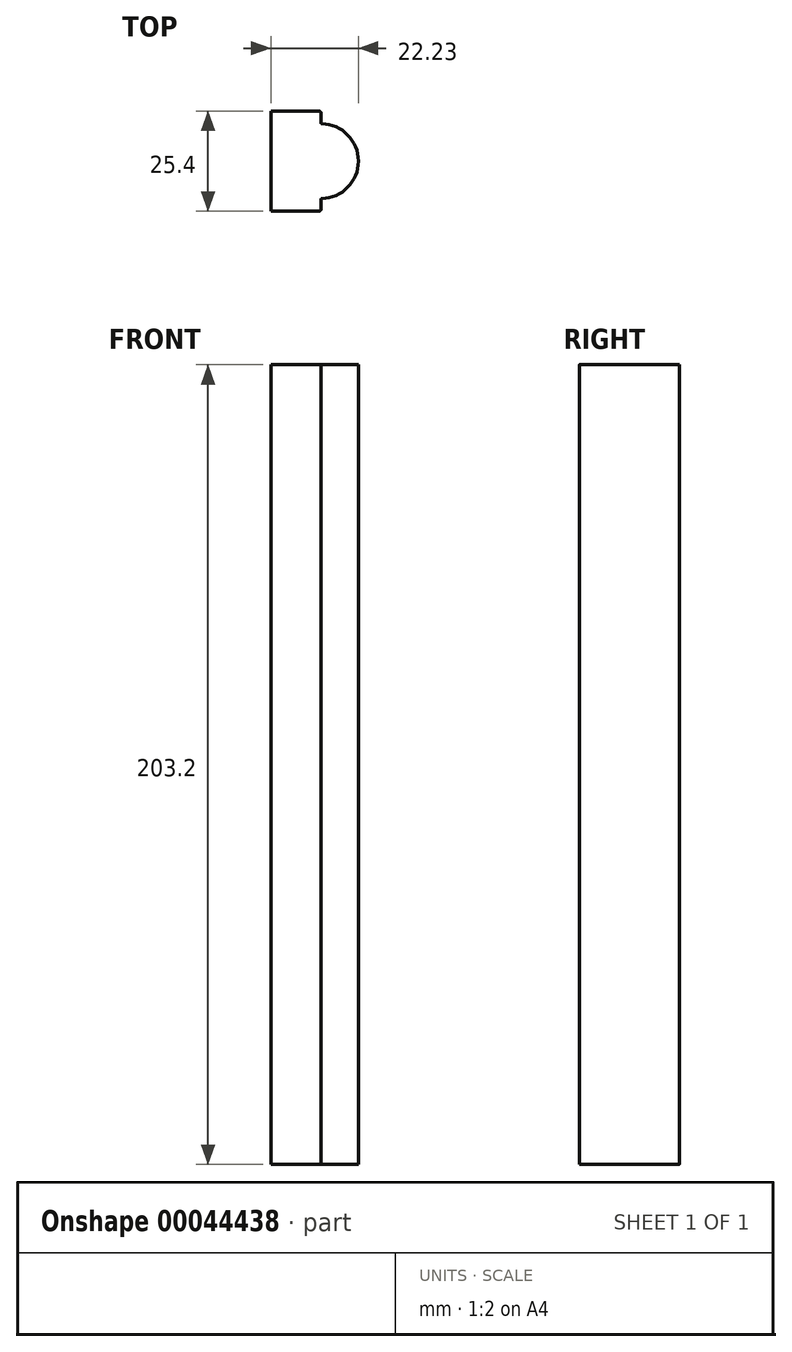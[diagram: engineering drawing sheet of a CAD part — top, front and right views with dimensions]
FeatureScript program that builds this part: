
annotation { "Feature Type Name" : "Feature", "Feature Type Description" : "" }
export const myFeature = defineFeature(function(context is Context, id is Id, definition is map)
    precondition{}
    {
        {
            var Q0;
            Q0=qCreatedBy(makeId("Top.planeOp"),FACE);
            var sketch = newSketch(context, id + "F0", { "sketchPlane" : qUnion([Q0])});
            skArc(sketch, "E0", {"start": v(0, -9.53) * mm, "mid": v(9.53, 0) * mm, "end": v(0, 9.53) * mm});
            skLineSegment(sketch, "E1", {"start": v(0, 9.53) * mm, "end": v(0, 12.7) * mm});
            skLineSegment(sketch, "E2", {"start": v(0, 12.7) * mm, "end": v(-12.7, 12.7) * mm});
            skLineSegment(sketch, "E3", {"start": v(-12.7, 12.7) * mm, "end": v(-12.7, -12.7) * mm});
            skLineSegment(sketch, "E4", {"start": v(-12.7, -12.7) * mm, "end": v(0, -12.7) * mm});
            skLineSegment(sketch, "E5", {"start": v(0, -12.7) * mm, "end": v(0, -9.53) * mm});
            skSolve(sketch);
        }
        {
            var Q0;
            Q0 = qSketchRegion(id + "F0", true);
            extrude(context, id + "F1", {"entities" : qUnion([Q0]), "depth" : 203.2 * mm});
        }
        {
            var Q0;
            Q0=makeQuery(id+"F1.opExtrude","SWEPT_EDGE",EDGE,{"disambiguationData":[OSD([sQuery(id+"F0.wireOp",EDGE,"E1"),sQuery(id+"F0.wireOp",EDGE,"E2")])]});
            var Q1;
            Q1=makeQuery(id+"F1.opExtrude","SWEPT_EDGE",EDGE,{"disambiguationData":[OSD([sQuery(id+"F0.wireOp",EDGE,"E4"),sQuery(id+"F0.wireOp",EDGE,"E5")])]});
            fillet(context, id + "F2", {"entities" : qUnion([Q0, Q1]), "radius" : 0.4 * mm, "tangentPropagation" : true, "allowEdgeOverflow" : false});
        }
        {
            var Q0;
            Q0=makeQuery(id+"F1.opExtrude","SWEPT_EDGE",EDGE,{"disambiguationData":[OSD([sQuery(id+"F0.wireOp",EDGE,"E0"),sQuery(id+"F0.wireOp",EDGE,"E1")])]});
            var Q1;
            Q1=makeQuery(id+"F1.opExtrude","SWEPT_EDGE",EDGE,{"disambiguationData":[OSD([sQuery(id+"F0.wireOp",EDGE,"E0"),sQuery(id+"F0.wireOp",EDGE,"E5")])]});
            fillet(context, id + "F3", {"entities" : qUnion([Q0, Q1]), "radius" : 0.24 * mm, "tangentPropagation" : true, "allowEdgeOverflow" : false});
        }
    });
